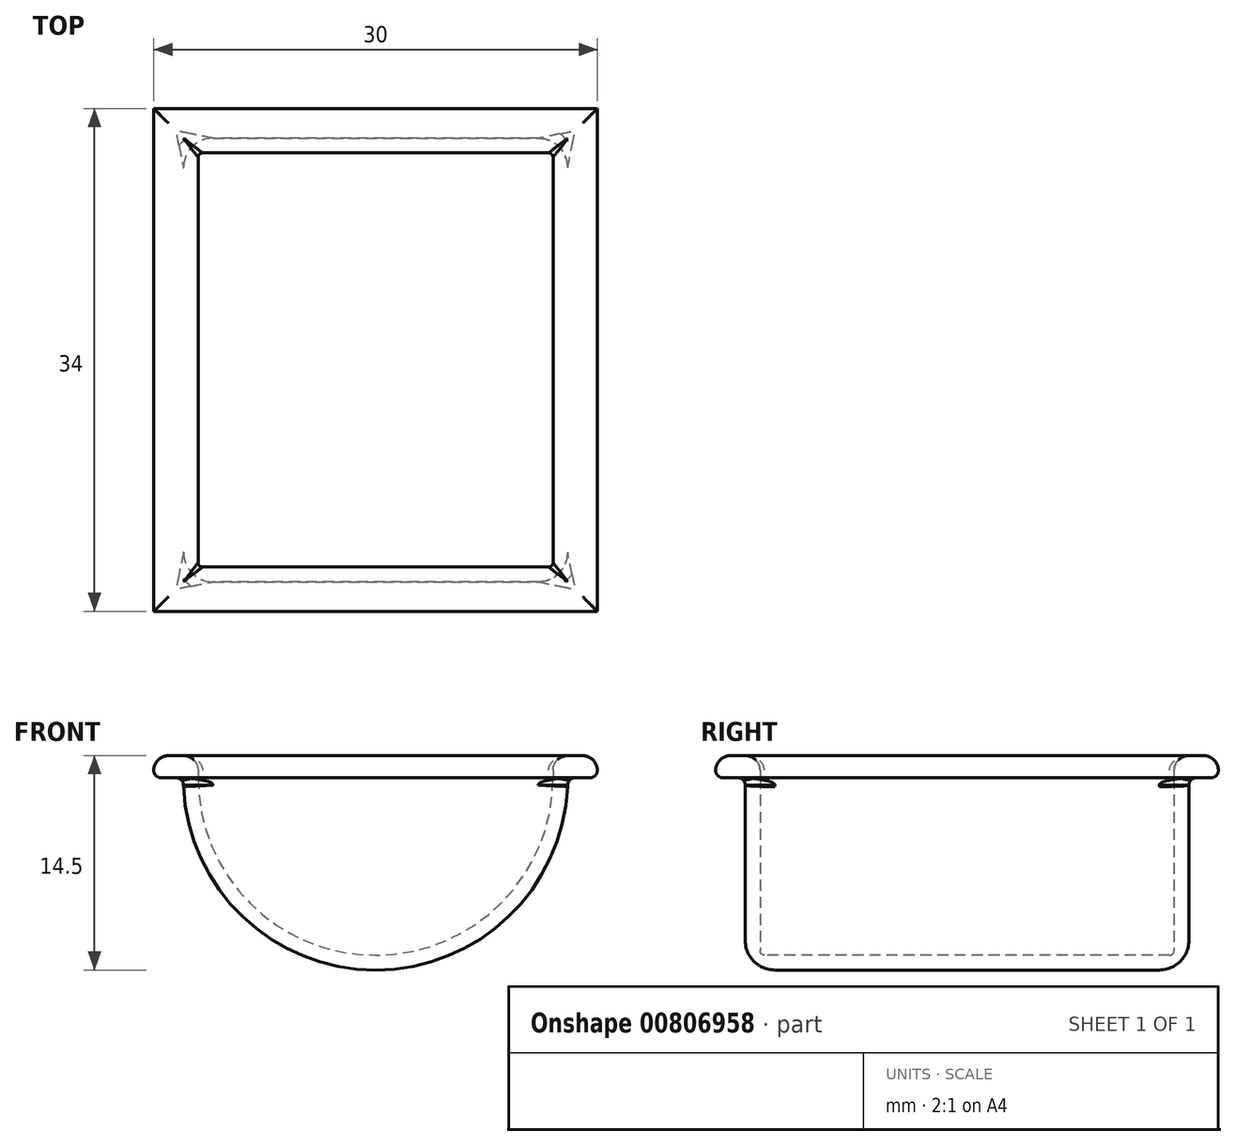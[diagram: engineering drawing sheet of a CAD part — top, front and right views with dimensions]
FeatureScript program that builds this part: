
annotation { "Feature Type Name" : "Feature", "Feature Type Description" : "" }
export const myFeature = defineFeature(function(context is Context, id is Id, definition is map)
    precondition{}
    {
        {
            var Q0;
            Q0=qCreatedBy(makeId("Front.planeOp"),FACE);
            var sketch = newSketch(context, id + "F0", { "sketchPlane" : qUnion([Q0])});
            skCircle(sketch, "E0", {"center": v(0, 0) * mm, "radius": 13 * mm});
            skSolve(sketch);
        }
        {
            var Q0;
            Q0=qSketchRegion(id+"F0",true);
            extrude(context, id + "F1", {"entities" : qUnion([Q0]), "depth" : 15 * mm, "offsetDistance" : 25 * mm, "hasSecondDirection" : true, "secondDirectionOppositeDirection" : true, "secondDirectionDepth" : 15 * mm});
        }
        {
            var Q0;
            Q0=qCreatedBy(makeId("Top.planeOp"),FACE);
            var sketch = newSketch(context, id + "F2", { "sketchPlane" : qUnion([Q0])});
            skLineSegment(sketch, "E1.bottom", {"start": v(13, -15) * mm, "end": v(-13, -15) * mm});
            skLineSegment(sketch, "E1.top", {"start": v(13, 15) * mm, "end": v(-13, 15) * mm});
            skLineSegment(sketch, "E1.left", {"start": v(13, -15) * mm, "end": v(13, 15) * mm});
            skLineSegment(sketch, "E1.right", {"start": v(-13, -15) * mm, "end": v(-13, 15) * mm});
            skPoint(sketch, "E1.middle", {"position": v(0, 0) * mm});
            skSolve(sketch);
        }
        {
            var Q0;
            Q0=qSketchRegion(id+"F2",true);
            extrude(context, id + "F3", {"entities" : qUnion([Q0]), "operationType" : NewBodyOperationType.REMOVE, "depth" : 25 * mm, "offsetDistance" : 25 * mm});
        }
        {
            var Q0;
            Q0=qCreatedBy(makeId("Front.planeOp"),FACE);
            var sketch = newSketch(context, id + "F4", { "sketchPlane" : qUnion([Q0])});
            skCircle(sketch, "E2", {"center": v(0, 0) * mm, "radius": 12 * mm});
            skSolve(sketch);
        }
        {
            var Q0;
            Q0=qSketchRegion(id+"F4",true);
            extrude(context, id + "F5", {"entities" : qUnion([Q0]), "operationType" : NewBodyOperationType.REMOVE, "oppositeDirection" : true, "depth" : 14 * mm, "offsetDistance" : 25 * mm, "hasSecondDirection" : true, "secondDirectionOppositeDirection" : false, "secondDirectionDepth" : 14 * mm});
        }
        {
            var Q0;
            Q0=makeQuery(id+"F3.boolean.opBoolean","COPY",FACE,{"derivedFrom":makeQuery(id+"F3.opExtrude","CAP_FACE",FACE,{"disambiguationData":[OSD([sQuery(id+"F2.wireOp",EDGE,"E1.bottom"),sQuery(id+"F2.wireOp",EDGE,"E1.top"),sQuery(id+"F2.wireOp",EDGE,"E1.left"),sQuery(id+"F2.wireOp",EDGE,"E1.right")])],"isStart":true})});
            var sketch = newSketch(context, id + "F6", { "sketchPlane" : qUnion([Q0])});
            skLineSegment(sketch, "E3.bottom", {"start": v(12, -14) * mm, "end": v(-12, -14) * mm});
            skLineSegment(sketch, "E3.top", {"start": v(12, 14) * mm, "end": v(-12, 14) * mm});
            skLineSegment(sketch, "E3.left", {"start": v(12, -14) * mm, "end": v(12, 14) * mm});
            skLineSegment(sketch, "E3.right", {"start": v(-12, -14) * mm, "end": v(-12, 14) * mm});
            skPoint(sketch, "E3.middle", {"position": v(0, 0) * mm});
            skLineSegment(sketch, "E4.bottom", {"start": v(15, -17) * mm, "end": v(-15, -17) * mm});
            skLineSegment(sketch, "E4.top", {"start": v(15, 17) * mm, "end": v(-15, 17) * mm});
            skLineSegment(sketch, "E4.left", {"start": v(15, -17) * mm, "end": v(15, 17) * mm});
            skLineSegment(sketch, "E4.right", {"start": v(-15, -17) * mm, "end": v(-15, 17) * mm});
            skSolve(sketch);
        }
        {
            var Q0;
            Q0=qSketchRegion(id+"F6",true);
            extrude(context, id + "F7", {"entities" : qUnion([Q0]), "operationType" : NewBodyOperationType.ADD, "depth" : 1.5 * mm, "offsetDistance" : 25 * mm});
        }
        {
            var Q0;
            Q0=makeQuery(id+"F7.opExtrude","CAP_FACE",FACE,{"disambiguationData":[OSD([sQuery(id+"F6.wireOp",EDGE,"E3.bottom"),sQuery(id+"F6.wireOp",EDGE,"E3.top"),sQuery(id+"F6.wireOp",EDGE,"E3.left"),sQuery(id+"F6.wireOp",EDGE,"E3.right"),sQuery(id+"F6.wireOp",EDGE,"E4.bottom"),sQuery(id+"F6.wireOp",EDGE,"E4.top"),sQuery(id+"F6.wireOp",EDGE,"E4.left"),sQuery(id+"F6.wireOp",EDGE,"E4.right")])],"isStart":false});
            fillet(context, id + "F8", {"entities" : qUnion([Q0]), "radius" : 1 * mm, "tangentPropagation" : true, "allowEdgeOverflow" : false});
        }
        {
            var Q0;
            Q0=makeQuery(id+"F7.opExtrude","CAP_FACE",FACE,{"disambiguationData":[OSD([sQuery(id+"F6.wireOp",EDGE,"E3.bottom"),sQuery(id+"F6.wireOp",EDGE,"E3.top"),sQuery(id+"F6.wireOp",EDGE,"E3.left"),sQuery(id+"F6.wireOp",EDGE,"E3.right"),sQuery(id+"F6.wireOp",EDGE,"E4.bottom"),sQuery(id+"F6.wireOp",EDGE,"E4.top"),sQuery(id+"F6.wireOp",EDGE,"E4.left"),sQuery(id+"F6.wireOp",EDGE,"E4.right")])],"isStart":true});
            fillet(context, id + "F9", {"entities" : qUnion([Q0]), "radius" : .5 * mm, "tangentPropagation" : true, "allowEdgeOverflow" : false});
        }
        {
            var Q0;
            Q0=makeQuery(id+"F1.opExtrude","CAP_EDGE",EDGE,{"disambiguationData":[OSD([sQuery(id+"F0.wireOp",EDGE,"E0")])],"isStart":false});
            var Q1;
            Q1=makeQuery(id+"F1.opExtrude","CAP_EDGE",EDGE,{"disambiguationData":[OSD([sQuery(id+"F0.wireOp",EDGE,"E0")])],"isStart":true});
            fillet(context, id + "F10", {"entities" : qUnion([Q0, Q1]), "radius" : 2 * mm, "tangentPropagation" : true, "allowEdgeOverflow" : false});
        }
        {
            var Q0;
            Q0=makeQuery(id+"F5.boolean.opBoolean","COPY",EDGE,{"derivedFrom":makeQuery(id+"F5.opExtrude","CAP_EDGE",EDGE,{"disambiguationData":[OSD([sQuery(id+"F4.wireOp",EDGE,"E2")])],"isStart":false})});
            var Q1;
            Q1=makeQuery(id+"F5.boolean.opBoolean","COPY",EDGE,{"derivedFrom":makeQuery(id+"F5.opExtrude","CAP_EDGE",EDGE,{"disambiguationData":[OSD([sQuery(id+"F4.wireOp",EDGE,"E2")])],"isStart":true})});
            fillet(context, id + "F11", {"entities" : qUnion([Q0, Q1]), "radius" : .3 * mm, "tangentPropagation" : true, "allowEdgeOverflow" : false});
        }
    });
